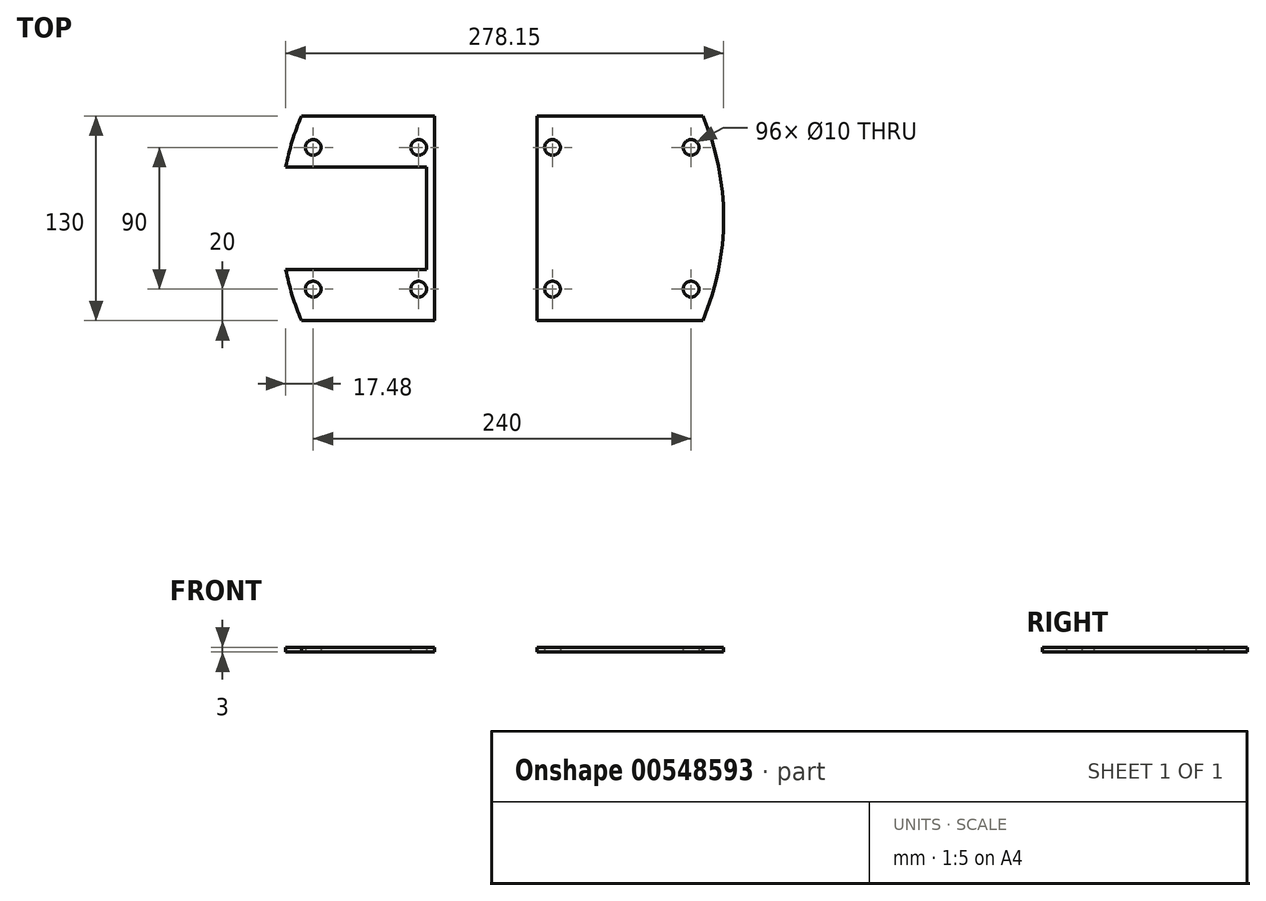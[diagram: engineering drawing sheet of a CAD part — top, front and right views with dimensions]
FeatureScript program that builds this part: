
annotation { "Feature Type Name" : "Feature", "Feature Type Description" : "" }
export const myFeature = defineFeature(function(context is Context, id is Id, definition is map)
    precondition{}
    {
        {
            var Q0;
            Q0=qCreatedBy(makeId("Top.planeOp"),FACE);
            var sketch = newSketch(context, id + "F0", { "sketchPlane" : qUnion([Q0])});
            skPoint(sketch, "E0.middle", {"position": v(0, 0) * mm});
            skArc(sketch, "E1", {"start": v(127.5, -65) * mm, "mid": v(140.67, 0) * mm, "end": v(127.5, 65) * mm});
            skArc(sketch, "E2.MirrorCS", {"start": v(-127.5, -65) * mm, "mid": v(-133.32, -49) * mm, "end": v(-137.48, -32.5) * mm});
            skCircle(sketch, "E3", {"center": v(120, 45) * mm, "radius": 5 * mm});
            skCircle(sketch, "E4.MirrorC", {"center": v(120, -45) * mm, "radius": 5 * mm});
            skCircle(sketch, "E5.MirrorC", {"center": v(-120, 45) * mm, "radius": 5 * mm});
            skCircle(sketch, "E6.MirrorC", {"center": v(-120, -45) * mm, "radius": 5 * mm});
            skLineSegment(sketch, "E7", {"start": v(-127.5, 65) * mm, "end": v(-43, 65) * mm});
            skLineSegment(sketch, "E8.MirrorCS", {"start": v(-127.5, -65) * mm, "end": v(127.5, -65) * mm});
            skArc(sketch, "E9.trimOffspring", {"start": v(-137.48, 32.5) * mm, "mid": v(-133.32, 49) * mm, "end": v(-127.5, 65) * mm});
            skLineSegment(sketch, "E10.left", {"start": v(-43, 65) * mm, "end": v(-43, -65) * mm});
            skLineSegment(sketch, "E10.right", {"start": v(22, 65) * mm, "end": v(22, -65) * mm});
            skLineSegment(sketch, "E11.trimOffspring", {"start": v(22, 65) * mm, "end": v(74.75, 65) * mm});
            skLineSegment(sketch, "E12", {"start": v(-43, 65) * mm, "end": v(-85.25, 65) * mm});
            skCircle(sketch, "E13.MirrorC", {"center": v(-53, 45) * mm, "radius": 5 * mm});
            skLineSegment(sketch, "E14", {"start": v(127.5, 65) * mm, "end": v(127.5, -65) * mm});
            skLineSegment(sketch, "E15", {"start": v(127.5, 65) * mm, "end": v(74.75, 65) * mm});
            skCircle(sketch, "E16.MirrorC", {"center": v(32, 45) * mm, "radius": 5 * mm});
            skCircle(sketch, "E17.MirrorC", {"center": v(-53, -45) * mm, "radius": 5 * mm});
            skCircle(sketch, "E18.MirrorC", {"center": v(32, -45) * mm, "radius": 5 * mm});
            skLineSegment(sketch, "E19", {"start": v(-48, 32.5) * mm, "end": v(-48, -32.5) * mm});
            skLineSegment(sketch, "E20", {"start": v(-137.48, 32.5) * mm, "end": v(-48, 32.5) * mm});
            skLineSegment(sketch, "E21", {"start": v(-137.48, -32.5) * mm, "end": v(-48, -32.5) * mm});
            skSolve(sketch);
        }
        {
            var Q0;
            Q0 = qSketchRegion(id + "F0", true);
            extrude(context, id + "F1", {"entities" : qUnion([Q0]), "depth" : 3 * mm, "offsetDistance" : 25 * mm});
        }
    });
